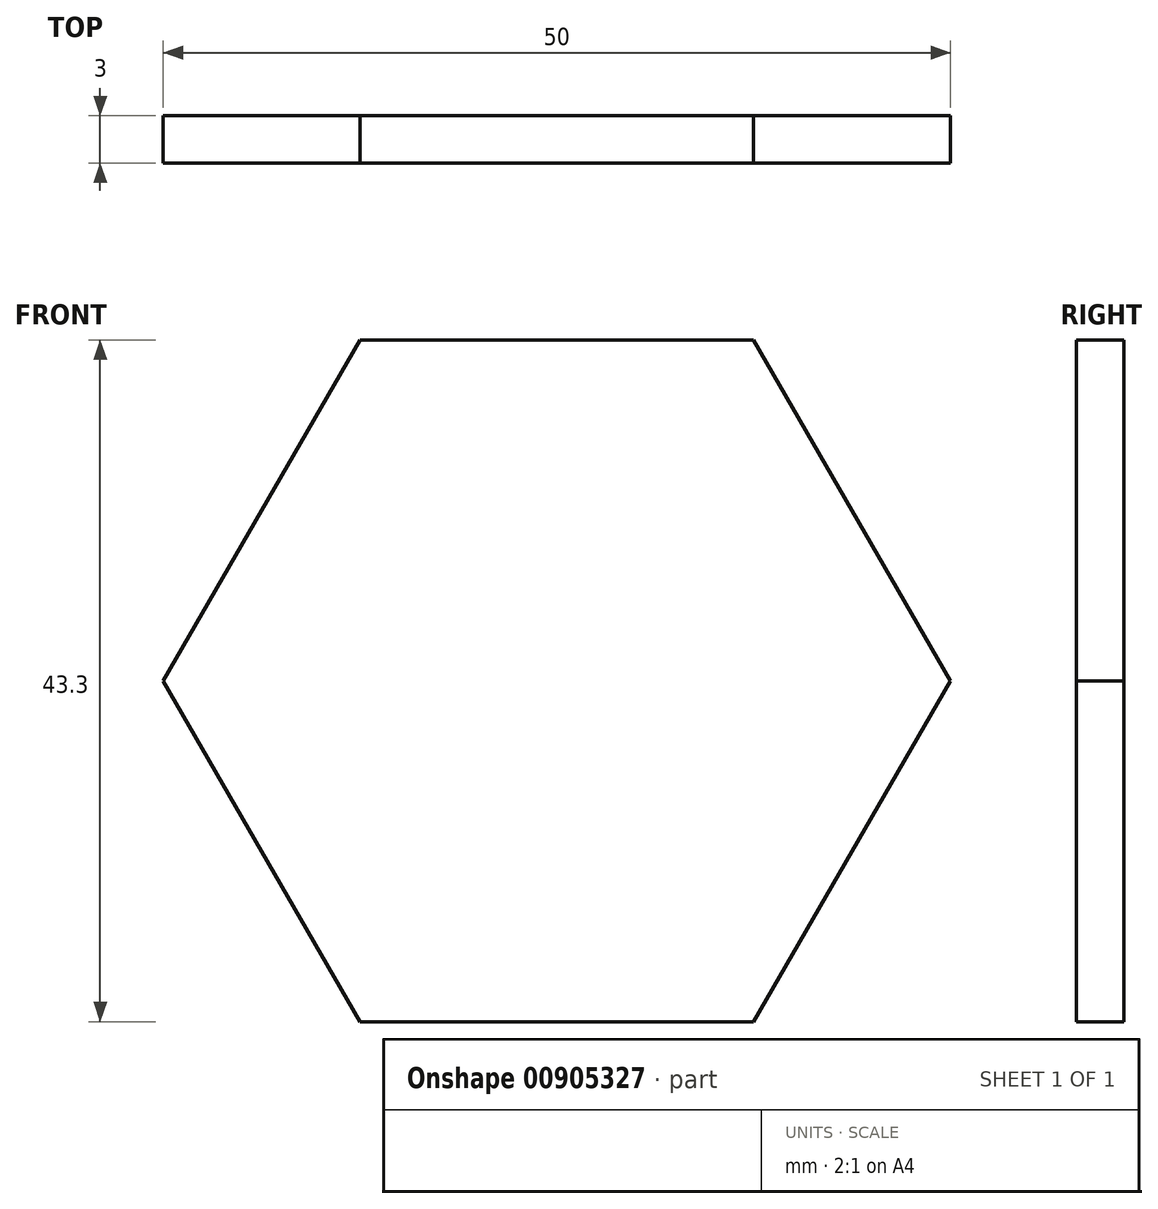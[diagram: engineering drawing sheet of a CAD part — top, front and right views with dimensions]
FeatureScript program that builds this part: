
annotation { "Feature Type Name" : "Feature", "Feature Type Description" : "" }
export const myFeature = defineFeature(function(context is Context, id is Id, definition is map)
    precondition{}
    {
        {
            var Q0;
            Q0=qCreatedBy(makeId("Front.planeOp"),FACE);
            var sketch = newSketch(context, id + "F0", { "sketchPlane" : qUnion([Q0])});
            skCircle(sketch, "E0.cCircle", {"center": v(0, 0) * mm, "radius": 25 * mm, "construction": true});
            skLineSegment(sketch, "E0.0", {"start": v(25, 0) * mm, "end": v(12.5, -21.65) * mm});
            skLineSegment(sketch, "E0.1", {"start": v(12.5, -21.65) * mm, "end": v(-12.5, -21.65) * mm});
            skLineSegment(sketch, "E0.2", {"start": v(-12.5, -21.65) * mm, "end": v(-25, 0) * mm});
            skLineSegment(sketch, "E0.3", {"start": v(-25, 0) * mm, "end": v(-12.5, 21.65) * mm});
            skLineSegment(sketch, "E0.4", {"start": v(-12.5, 21.65) * mm, "end": v(12.5, 21.65) * mm});
            skLineSegment(sketch, "E0.5", {"start": v(12.5, 21.65) * mm, "end": v(25, 0) * mm});
            skSolve(sketch);
        }
        {
            var Q0;
            Q0=makeQuery(id+"F0.imprint","IMPRINT",FACE,{"disambiguationData":[TD([[makeQuery(id+"F0.imprint","IMPRINT",EDGE,{"derivedFrom":sQuery(id+"F0.wireOp",EDGE,"E0.0")}),-1.0]])]});
            extrude(context, id + "F1", {"entities" : qUnion([Q0]), "depth" : 3 * mm, "offsetDistance" : 25.4 * mm});
        }
    });
